# Revit family: Domotics-DomesticRanges-GEWISS-CHORUS_DATA-SOCKET-OUTLET_TV-SAT_2M
name_source: partatom
category: Apparecchi elettrici
revit_build: Autodesk Revit 2016 (Build: 20161004_0715(x64)
units: mm (PartAtom-declared; Revit-internal decimal feet)

## family parameters
Condiviso = Sì
Host = Superficie
Mantenere orientamento annotazione = Sì
Punto di calcolo locali = Sì
Quota connettore circolare = Usa diametro
Taglio con vuoti quando caricato = Sì
Tipo di parte = Normale

## types (3) — shared parameters
Carico apparente = 0 VA
Catalogue = DOMOTICS
Catalogue Range = CHORUS - DOMESTIC RANGE
IDF = cc36dfe0-52ef-4d56-bdf4-90c70f6859ea
IDT = 208dc7ca-ed91-470d-b318-df14e7277599
Immagine tipo = GW14377.jpg
N. poli = 1
Produttore = GEWISS S.p.A.
Prospetto di default = 1219 mm
Technical sheet = https://www.gewiss.com
Tipo_ = SYSTEM PRESE TV-SAT_GENERICO : GW titanio
URL = https://www.gewiss.com
Version file RFA = 19.0
Volt = 230 V

## per-type parameters (varying)
| type | Descrizione | EAN code | Electrocod | Modello |
| GW12377 - TV/SAT SOCKET 2M DIRECT F.CONN F BLACK | TV/SAT SOCKET 2M DIRECT F.CONN F BLACK | 8011564823747 | 3721 | GW12377 |
| GW10377 - TV/SAT SOCKET 2M DIRECT F.CONN F WHITE | TV/SAT SOCKET 2M DIRECT F.CONN F WHITE | 8011564823730 | 3720 | GW10377 |
| GW14377 - TV/SAT SOCKET 2M DIRECT F.CONN F TIT. | TV/SAT SOCKET 2M DIRECT F.CONN F TIT. | 8011564823754 | 3720 | GW14377 |

## geometry (parser evidence)
native form markers: Sweep x1
no freeform markers — native parametric forms only
